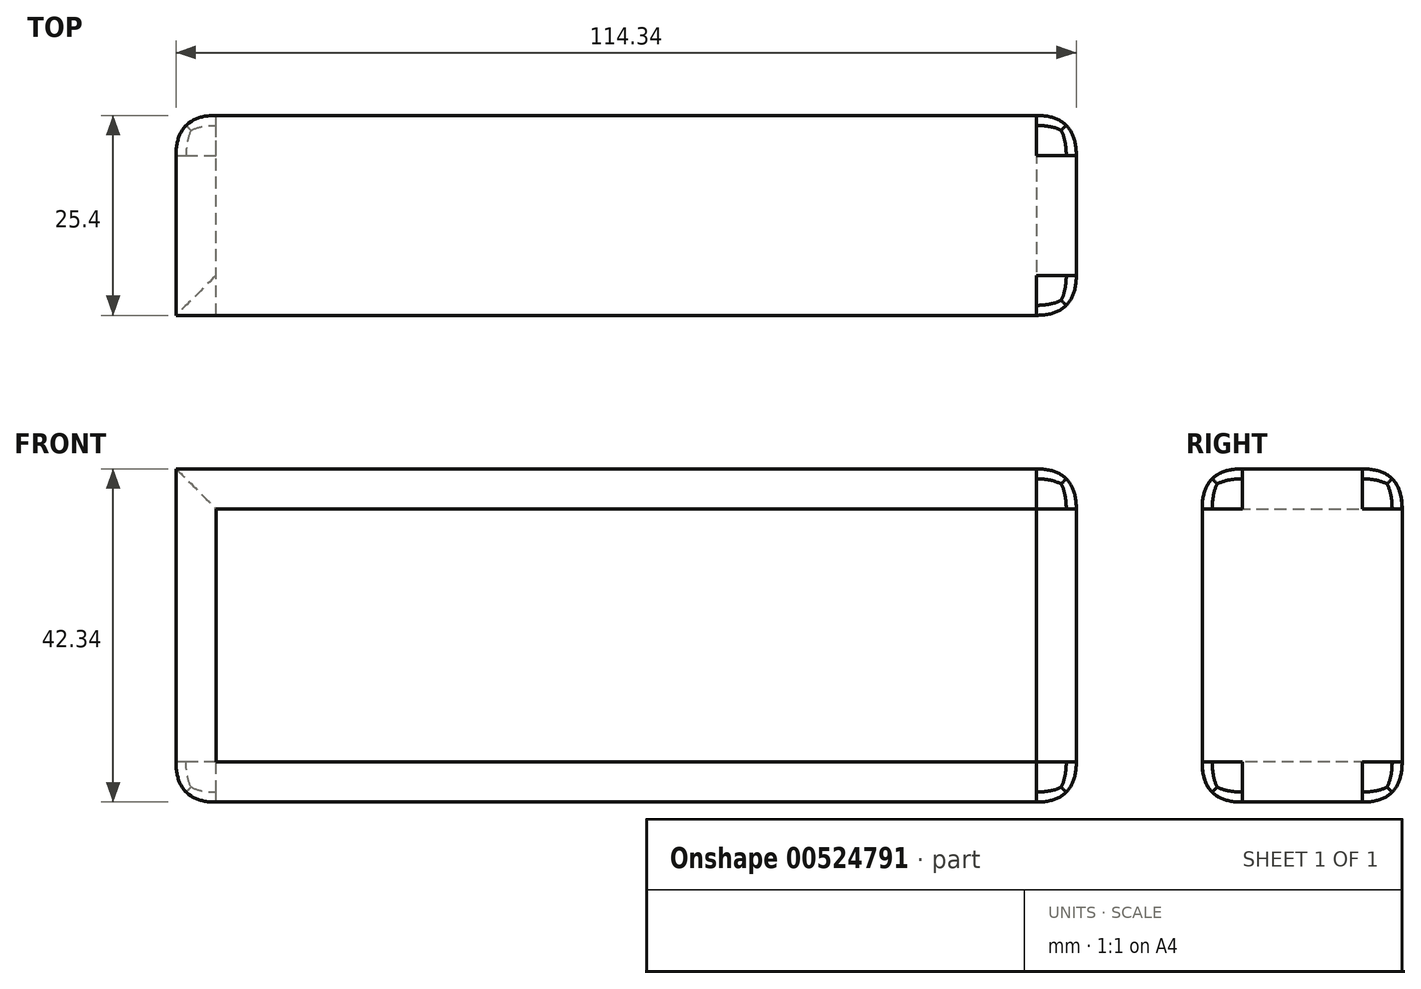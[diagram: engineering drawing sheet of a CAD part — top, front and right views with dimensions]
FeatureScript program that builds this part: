
annotation { "Feature Type Name" : "Feature", "Feature Type Description" : "" }
export const myFeature = defineFeature(function(context is Context, id is Id, definition is map)
    precondition{}
    {
        {
            var Q0;
            Q0=qCreatedBy(makeId("Front.planeOp"),FACE);
            var sketch = newSketch(context, id + "F0", { "sketchPlane" : qUnion([Q0])});
            skLineSegment(sketch, "E0.bottom", {"start": v(-57.17, 21.17) * mm, "end": v(57.17, 21.17) * mm});
            skLineSegment(sketch, "E0.top", {"start": v(-57.17, -21.17) * mm, "end": v(57.17, -21.17) * mm});
            skLineSegment(sketch, "E0.left", {"start": v(-57.17, 21.17) * mm, "end": v(-57.17, -21.17) * mm});
            skLineSegment(sketch, "E0.right", {"start": v(57.17, 21.17) * mm, "end": v(57.17, -21.17) * mm});
            skPoint(sketch, "E0.middle", {"position": v(0, 0) * mm});
            skSolve(sketch);
        }
        {
            var Q0;
            Q0=makeQuery(id+"F0.imprint","IMPRINT",FACE,{"disambiguationData":[TD([[makeQuery(id+"F0.imprint","IMPRINT",EDGE,{"derivedFrom":sQuery(id+"F0.wireOp",EDGE,"E0.bottom")}),-1.0]])]});
            extrude(context, id + "F1", {"entities" : qUnion([Q0]), "oppositeDirection" : true, "depth" : 25.4 * mm, "offsetDistance" : 25.4 * mm});
        }
        {
            var Q0;
            Q0=makeQuery(id+"F1.opExtrude","CAP_EDGE",EDGE,{"disambiguationData":[OSD([sQuery(id+"F0.wireOp",EDGE,"E0.bottom")])],"isStart":true});
            var Q1;
            Q1=makeQuery(id+"F1.opExtrude","SWEPT_EDGE",EDGE,{"disambiguationData":[OSD([sQuery(id+"F0.wireOp",EDGE,"E0.bottom"),sQuery(id+"F0.wireOp",EDGE,"E0.right")])]});
            var Q2;
            Q2=makeQuery(id+"F1.opExtrude","CAP_FACE",FACE,{"disambiguationData":[OSD([sQuery(id+"F0.wireOp",EDGE,"E0.bottom"),sQuery(id+"F0.wireOp",EDGE,"E0.top"),sQuery(id+"F0.wireOp",EDGE,"E0.left"),sQuery(id+"F0.wireOp",EDGE,"E0.right")])],"isStart":false});
            var Q3;
            Q3=makeQuery(id+"F1.opExtrude","SWEPT_EDGE",EDGE,{"disambiguationData":[OSD([sQuery(id+"F0.wireOp",EDGE,"E0.top"),sQuery(id+"F0.wireOp",EDGE,"E0.right")])]});
            var Q4;
            Q4=makeQuery(id+"F1.opExtrude","SWEPT_FACE",FACE,{"disambiguationData":[OSD([sQuery(id+"F0.wireOp",EDGE,"E0.top")])]});
            var Q5;
            Q5=makeQuery(id+"F1.opExtrude","CAP_EDGE",EDGE,{"disambiguationData":[OSD([sQuery(id+"F0.wireOp",EDGE,"E0.bottom")])],"isStart":false});
            var Q6;
            Q6=makeQuery(id+"F1.opExtrude","SWEPT_FACE",FACE,{"disambiguationData":[OSD([sQuery(id+"F0.wireOp",EDGE,"E0.right")])]});
            var Q7;
            Q7=makeQuery(id+"F1.opExtrude","CAP_EDGE",EDGE,{"disambiguationData":[OSD([sQuery(id+"F0.wireOp",EDGE,"E0.left")])],"isStart":false});
            var Q8;
            Q8=makeQuery(id+"F1.opExtrude","CAP_EDGE",EDGE,{"disambiguationData":[OSD([sQuery(id+"F0.wireOp",EDGE,"E0.right")])],"isStart":false});
            var Q9;
            Q9=makeQuery(id+"F1.opExtrude","SWEPT_EDGE",EDGE,{"disambiguationData":[OSD([sQuery(id+"F0.wireOp",EDGE,"E0.top"),sQuery(id+"F0.wireOp",EDGE,"E0.left")])]});
            var Q10;
            Q10=makeQuery(id+"F1.opExtrude","CAP_EDGE",EDGE,{"disambiguationData":[OSD([sQuery(id+"F0.wireOp",EDGE,"E0.top")])],"isStart":true});
            var Q11;
            Q11=makeQuery(id+"F1.opExtrude","CAP_EDGE",EDGE,{"disambiguationData":[OSD([sQuery(id+"F0.wireOp",EDGE,"E0.top")])],"isStart":false});
            var Q12;
            Q12=makeQuery(id+"F1.opExtrude","CAP_EDGE",EDGE,{"disambiguationData":[OSD([sQuery(id+"F0.wireOp",EDGE,"E0.right")])],"isStart":true});
            fillet(context, id + "F2", {"entities" : qUnion([Q0, Q1, Q2, Q3, Q4, Q5, Q6, Q7, Q8, Q9, Q10, Q11, Q12]), "radius" : 5.08 * mm, "tangentPropagation" : true, "rho" : 0.5, "crossSection" : FilletCrossSection.CONIC, "allowEdgeOverflow" : false});
        }
        {
            var Q0;
            Q0=makeQuery(id+"F1.opExtrude","CAP_FACE",FACE,{"disambiguationData":[OSD([sQuery(id+"F0.wireOp",EDGE,"E0.bottom"),sQuery(id+"F0.wireOp",EDGE,"E0.top"),sQuery(id+"F0.wireOp",EDGE,"E0.left"),sQuery(id+"F0.wireOp",EDGE,"E0.right")])],"isStart":false});
            var sketch = newSketch(context, id + "F3", { "sketchPlane" : qUnion([Q0])});
            skSolve(sketch);
        }
        {
            var Q0;
            {var subQ0=sQuery(id+"F0.wireOp",EDGE,"E0.right");var subQ1=sQuery(id+"F0.wireOp",EDGE,"E0.left");var subQ2=sQuery(id+"F0.wireOp",EDGE,"E0.top");var subQ3=sQuery(id+"F0.wireOp",EDGE,"E0.bottom");var subQ4=makeQuery(id+"F1.opExtrude","CAP_FACE",FACE,{"disambiguationData":[OSD([subQ3,subQ2,subQ1,subQ0])],"isStart":false});Q0=makeQuery(id+"F3.imprint","IMPRINT",FACE,{"disambiguationData":[TD([[makeQuery(id+"F3.imprint","IMPRINT",EDGE,{"derivedFrom":makeQuery(id+"F2.opFillet","BLEND_EDGE",EDGE,{"blendedFrom":[makeQuery(id+"F1.opExtrude","CAP_EDGE",EDGE,{"disambiguationData":[OSD([subQ3])],"isStart":false}),subQ4],"blendedInto":[subQ4]})}),1.0]])]});}
            extrude(context, id + "F4", {"entities" : qUnion([Q0]), "operationType" : NewBodyOperationType.ADD, "oppositeDirection" : true, "depth" : 127 * mm, "offsetDistance" : 25.4 * mm});
        }
        {
            var Q0;
            Q0=makeQuery(id+"F1.opExtrude","CAP_FACE",FACE,{"disambiguationData":[OSD([sQuery(id+"F0.wireOp",EDGE,"E0.bottom"),sQuery(id+"F0.wireOp",EDGE,"E0.top"),sQuery(id+"F0.wireOp",EDGE,"E0.left"),sQuery(id+"F0.wireOp",EDGE,"E0.right")])],"isStart":false});
            var sketch = newSketch(context, id + "F5", { "sketchPlane" : qUnion([Q0])});
            skSolve(sketch);
        }
        {
            var Q0;
            {var subQ0=sQuery(id+"F0.wireOp",EDGE,"E0.right");var subQ1=sQuery(id+"F0.wireOp",EDGE,"E0.left");var subQ2=sQuery(id+"F0.wireOp",EDGE,"E0.top");var subQ3=sQuery(id+"F0.wireOp",EDGE,"E0.bottom");var subQ4=makeQuery(id+"F1.opExtrude","CAP_FACE",FACE,{"disambiguationData":[OSD([subQ3,subQ2,subQ1,subQ0])],"isStart":false});Q0=makeQuery(id+"F5.imprint","IMPRINT",FACE,{"disambiguationData":[TD([[makeQuery(id+"F5.imprint","IMPRINT",EDGE,{"derivedFrom":makeQuery(id+"F2.opFillet","BLEND_EDGE",EDGE,{"blendedFrom":[makeQuery(id+"F1.opExtrude","CAP_EDGE",EDGE,{"disambiguationData":[OSD([subQ3])],"isStart":false}),subQ4],"blendedInto":[subQ4]})}),1.0]])]});}
            extrude(context, id + "F6", {"entities" : qUnion([Q0]), "operationType" : NewBodyOperationType.REMOVE, "depth" : 25.4 * mm, "offsetDistance" : 25.4 * mm});
        }
        {
            var Q0;
            Q0=makeQuery(id+"F1.opExtrude","CAP_FACE",FACE,{"disambiguationData":[OSD([sQuery(id+"F0.wireOp",EDGE,"E0.bottom"),sQuery(id+"F0.wireOp",EDGE,"E0.top"),sQuery(id+"F0.wireOp",EDGE,"E0.left"),sQuery(id+"F0.wireOp",EDGE,"E0.right")])],"isStart":false});
            extrude(context, id + "F7", {"entities" : qUnion([Q0]), "operationType" : NewBodyOperationType.REMOVE, "oppositeDirection" : true, "depth" : 127 * mm, "offsetDistance" : 25.4 * mm});
        }
    });
